# Revit family: Doors-Overhead_Rapid-HöRMANN-SR9000_L
name_source: partatom
category: Doors
revit_build: Autodesk Revit 2015 (Build: 20160512_1515(x64)
units: mm (PartAtom-declared; Revit-internal decimal feet)

## types (1)
- Doors-Overhead_Rapid-HöRMANN-SR9000_L
    Acoustical Rating = STC-Rw 26; OITC 24
    Ambient Temperature = 40 °C
    Analytic Construction = <None>
    Application = Exterior / Interior
    Assembly Code = B2030410
    Bracket Support Materials = Steel, Hot-dipped Galvanized
    Brochure URL = http://www.hormann-flexon.com
    CAD URL = http://www.hormann-flexon.com
    CSI Masterformat 2014 = 08 33 23.13 - Overhead Rapid Coiling Doors
    Country of Origin = United States of America
    Cut Sheet URL = Coming Soon
    Decotherm® Insulated Slat Materials = Steel, Hot-dipped Galvanized; Polyurethane Foam Insulation
    Description = Overhead Coiling Doors
    Disconnect = Fuse: 16amp Class K
    Draft Seal Matetrial = PVC, Filament Brush, Black
    Emergency Opening = Operation via Chain Hoist
    Enclosure Protection Category Control Box = NEMA 4, UL/cUL Listed
    Enclosure Protection Category Motor = NEMA 3
    Fire Rating = Non-Rated, Non-Conforming Exit
    Freight Class = 70
    Full Load Amps = 6 A
    Guide Track Design = Compact Profile, Interior Mount Only
    Guide Track Material = Aluminum, Anodized
    Hardware Set = Hardware is Manufacturer furnished.
    Heat Transfer Coefficient (U) = 0.125 BTU/(h·ft²·°F)
    Hood Material = Steel, Hot-dipped Galvanized
    Horse Power = 2 hp
    Installation Manual URL = http://www.hormann-flexon.com
    Insulation Class - ICL = F
    Keynote = 08 33 23.13
    LEED Credit = MR Credit 2; MR Credit 4; EQ Credit 5
    Manufacturer = Hörmann Flexon, LLC.
    Manufacturer Disclaimer = We believe this information to be the best currently available, and is offered only as a possible suggestion and guideline in design exploration you may undertake. It is subject to revision without notice. We make no guarantee of results and assume no obligation or liability whatsoever in connection with this information. Confirm all information with the Manufacturer prior to implementation.
    Manufacturer Location = Starpointe Business Park, 117 Starpointe Blvd. Burgettstown, PA 15021-9506
    Model = Steel Ranger™ 9000 L
    Motor Frequency = 60 Hz
    Mounting Diagram URL = Coming Soon
    Operating Speed = Up to 45 in per second opening, and 30 in per second closing
    Operation = Rapid Overhead Coiling
    Operator_Motor = GfA Elektromaten - F18
    PDF URL = http://www.hormann-flexon.com
    Power Rating = 2 hp
    Product Options = -
    Publish Date = April 29, 2016
    RPM = 1730
    Representative Disclaimer = Hörmann Flexon products are sold and installed through a nationwide independent network of distributors.
    Roll Tube = Steel, Hot-dipped Galvanized
    Service Factor = 2 SF
    Size Range = Up to 16'-0" wide by 14'-0" high
    Sizing Disclaimer = Openings up to sixteen feet wide by fourteen feet high are standard construction. Please consult Hörmann Flexon for larger sizes.
    Solar Heat Gain Coefficient = 0.75
    Specifications URL = http://www.hormann-flexon.com
    Standard Power Requirement = 230 V or 480 V, 3 PH, 60 Hz
    Thermal Resistance (R) = 8.0000 (h·ft²·°F)/BTU
    Thickness = 0' - 0 11/16"
    Type Comments = Revolutionary design, Legendary Hörmann quality built-in. A class above traditional rolling steel doors.
    URL = http://www.hormann-flexon.com
    Version Number = v. 000 Beta
    Vision Material = Double Pane - Polycarbonate, Clear, DURATEC® Coating
    Visual Light Transmittance = 0.91
    Wall Closure = By host
    Warranty = 5 & 2 Limited Warranty: The motor (excluding catch) and panel material are guarranteed against defects in materials and workmanship for a period of 5 years. All other mechanical and electrical components are warranted against defects for a period of 2 full years.
    Wind Load Resistance = 20 psf / 88 mph
    _Panel Surface (Both Sides) = Micrograin™ Texture
    ifcName = ifcDoor

## geometry (parser evidence)
native form markers: Blend x4, Sweep x68
no freeform markers — native parametric forms only
